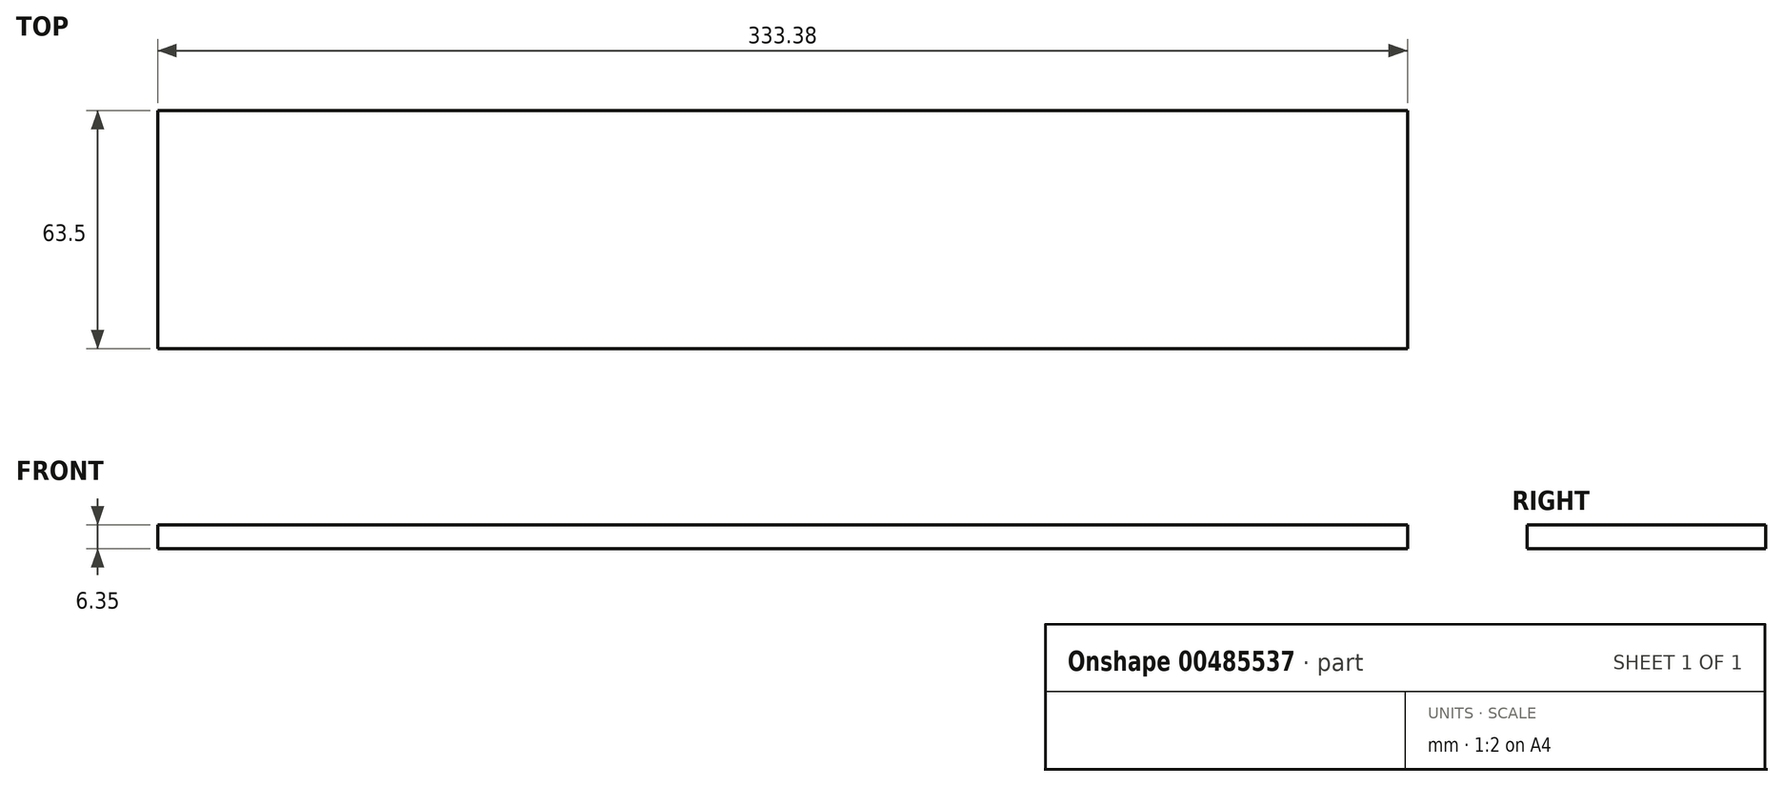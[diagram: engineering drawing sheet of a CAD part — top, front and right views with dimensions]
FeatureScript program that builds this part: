
annotation { "Feature Type Name" : "Feature", "Feature Type Description" : "" }
export const myFeature = defineFeature(function(context is Context, id is Id, definition is map)
    precondition{}
    {
        {
            var Q0;
            Q0=qCreatedBy(makeId("Top.planeOp"),FACE);
            var sketch = newSketch(context, id + "F0", { "sketchPlane" : qUnion([Q0])});
            skLineSegment(sketch, "E0.bottom", {"start": v(166.69, 31.75) * mm, "end": v(-166.69, 31.75) * mm});
            skLineSegment(sketch, "E0.top", {"start": v(166.69, -31.75) * mm, "end": v(-166.69, -31.75) * mm});
            skLineSegment(sketch, "E0.left", {"start": v(166.69, 31.75) * mm, "end": v(166.69, -31.75) * mm});
            skLineSegment(sketch, "E0.right", {"start": v(-166.69, 31.75) * mm, "end": v(-166.69, -31.75) * mm});
            skPoint(sketch, "E0.middle", {"position": v(0, 0) * mm});
            skSolve(sketch);
        }
        {
            var Q0;
            Q0 = qSketchRegion(id + "F0", true);
            extrude(context, id + "F1", {"entities" : qUnion([Q0]), "depth" : 6.35 * mm});
        }
    });
